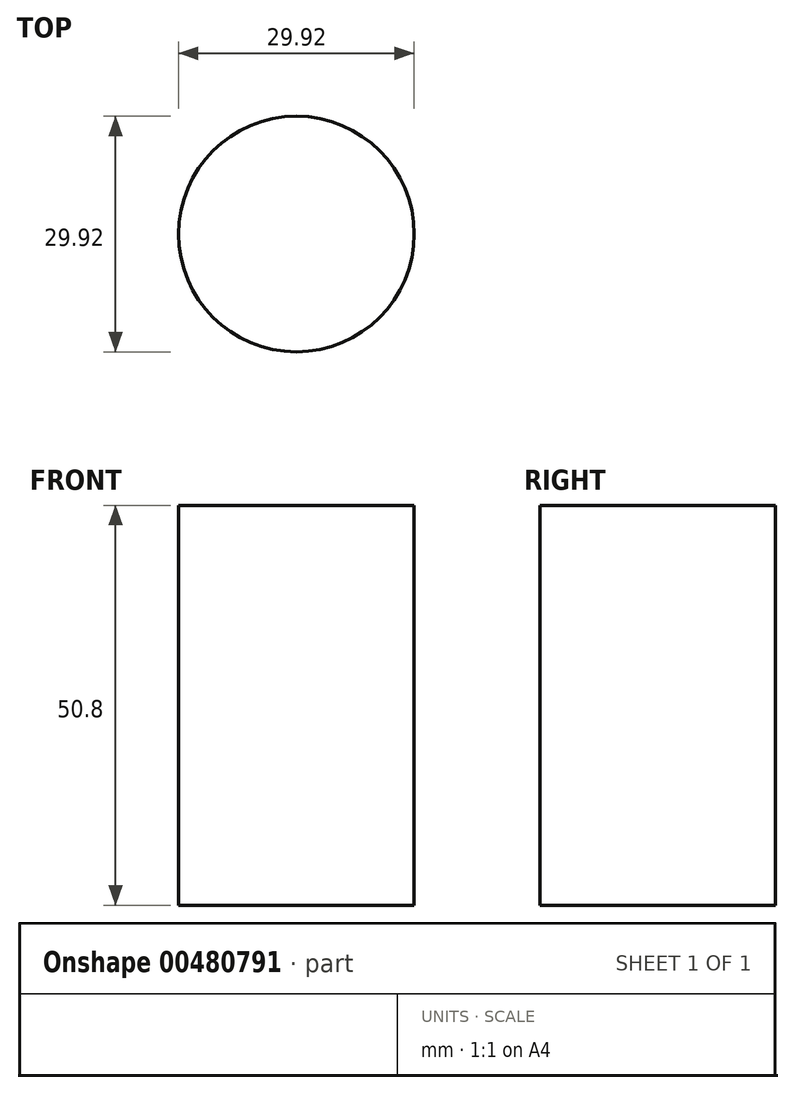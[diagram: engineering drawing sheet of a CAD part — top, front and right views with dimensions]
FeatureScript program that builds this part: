
annotation { "Feature Type Name" : "Feature", "Feature Type Description" : "" }
export const myFeature = defineFeature(function(context is Context, id is Id, definition is map)
    precondition{}
    {
        {
            var Q0;
            Q0=qCreatedBy(makeId("Top.planeOp"),FACE);
            var sketch = newSketch(context, id + "F0", { "sketchPlane" : qUnion([Q0])});
            skCircle(sketch, "E0", {"center": v(0, 0) * mm, "radius": 14.96 * mm});
            skSolve(sketch);
        }
        {
            var Q0;
            Q0=makeQuery(id+"F0.imprint","IMPRINT",FACE,{"disambiguationData":[TD([[makeQuery(id+"F0.imprint","IMPRINT",EDGE,{"derivedFrom":sQuery(id+"F0.wireOp",EDGE,"E0")}),1.0]])]});
            extrude(context, id + "F1", {"entities" : qUnion([Q0]), "depth" : 50.8 * mm, "offsetDistance" : 25.4 * mm});
        }
    });
